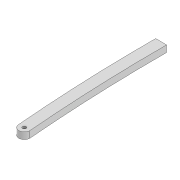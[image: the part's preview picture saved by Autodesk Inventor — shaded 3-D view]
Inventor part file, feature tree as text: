
AUTODESK INVENTOR PART (.ipt)
format: ipt  version: 2022 (Build 260153000, 153)  size: 100,352 bytes
history: native  units: mm
features: extrude x2, sketch x2
ambient origin geometry x8: Origin, YZ Plane, XZ Plane, XY Plane, X Axis, Y Axis, Z Axis, Center Point
bodies: Solid1 (feature_tree)
feature tree (4):
  extrude  "Extrusion1"  Depth=3.3mm
  extrude  "Extrusion2"  Depth=10.0mm
  sketch  "Sketch1"  dims[d0=3.3mm d1=3.3mm]
  sketch  "Sketch2"  dims[d2=10.0mm d3=253.429mm d6=6.0mm d7=0.0mm d16=1500.0mm d17=1500.0mm d18=10.0mm d19=0.0mm]
